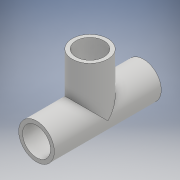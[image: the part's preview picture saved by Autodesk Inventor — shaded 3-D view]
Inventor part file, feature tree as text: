
AUTODESK INVENTOR PART (.ipt)
format: ipt  version: 2017 (Build 210142000, 142)  size: 116,224 bytes
history: native  units: mm
features: extrude x2, sketch x2, plane x1, shell x1
ambient origin geometry x8: Origin, YZ Plane, XZ Plane, XY Plane, X Axis, Y Axis, Z Axis, Center Point
bodies: Solid1 (feature_tree)
feature tree (6):
  extrude  "Extrusion1"  Depth=84.0mm TaperAngle=0.0deg
  plane  "Work Plane1"
  extrude  "Extrusion2"  Depth=42.0mm
  shell  "Shell1"  Thickness=100.0mm
  sketch  "Sketch1"  dims[d0=28.0mm d1=84.0mm d2=0.0mm]
  sketch  "Sketch2"  dims[d3=42.0mm d4=28.0mm d5=100.0mm d6=0.0mm d7=3.0mm]
